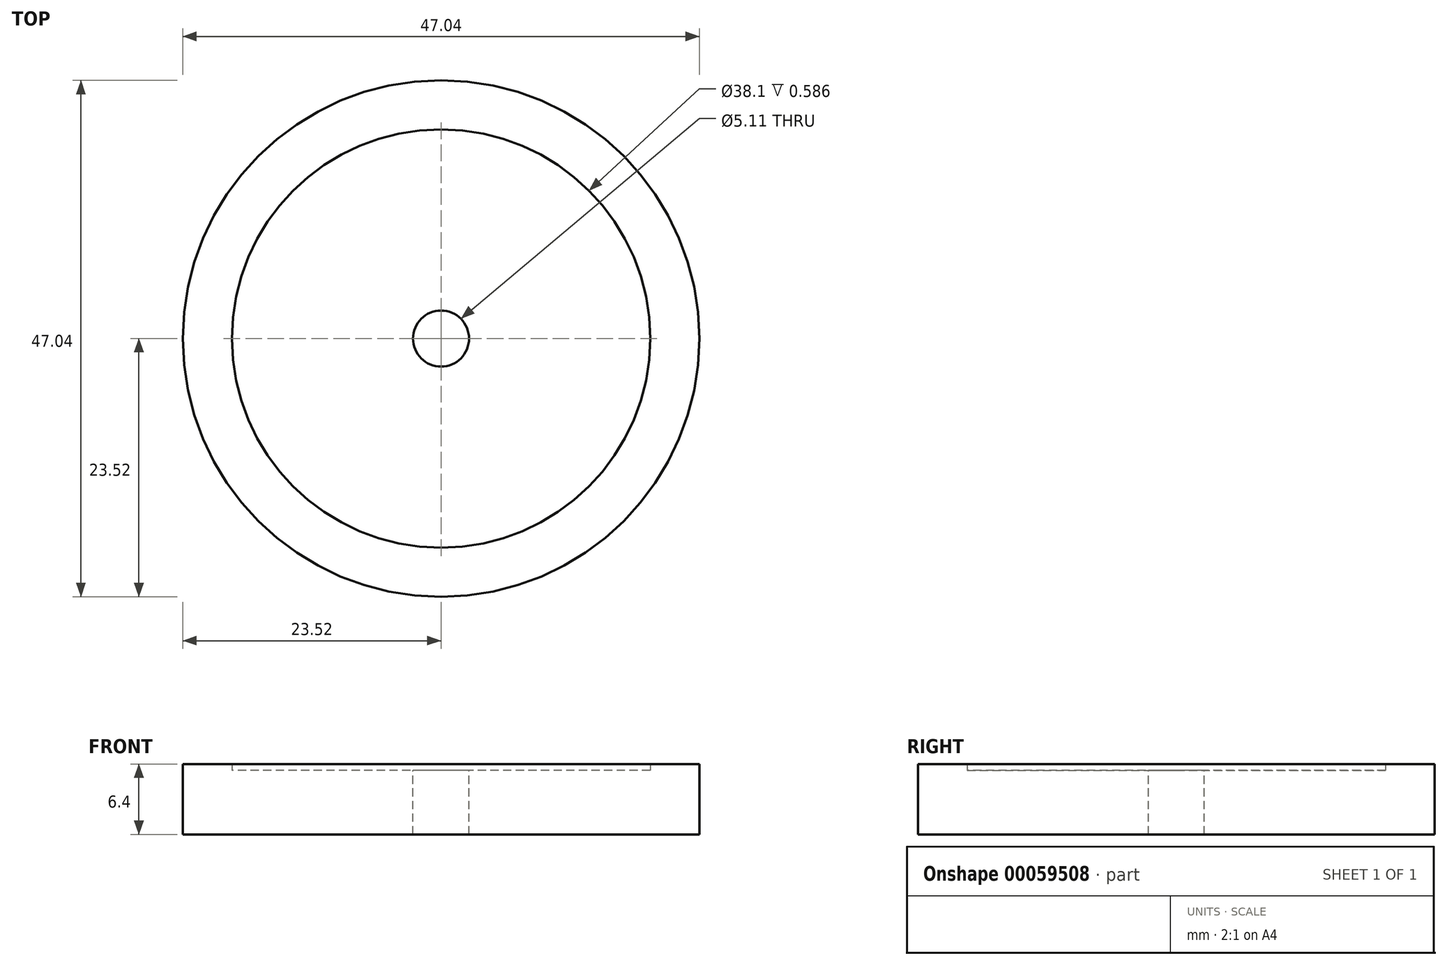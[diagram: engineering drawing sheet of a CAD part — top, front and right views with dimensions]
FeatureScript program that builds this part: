
annotation { "Feature Type Name" : "Feature", "Feature Type Description" : "" }
export const myFeature = defineFeature(function(context is Context, id is Id, definition is map)
    precondition{}
    {
        {
            var Q0;
            Q0=qCreatedBy(makeId("Top.planeOp"),FACE);
            var sketch = newSketch(context, id + "F0", { "sketchPlane" : qUnion([Q0])});
            skCircle(sketch, "E0", {"center": v(0, 0) * mm, "radius": 23.52 * mm});
            skCircle(sketch, "E1", {"center": v(0, 0) * mm, "radius": 19.05 * mm});
            skSolve(sketch);
        }
        {
            var Q0;
            Q0=makeQuery(id+"F0.imprint","IMPRINT",FACE,{"disambiguationData":[TD([[makeQuery(id+"F0.imprint","IMPRINT",EDGE,{"derivedFrom":sQuery(id+"F0.wireOp",EDGE,"E0")}),1.0]])]});
            extrude(context, id + "F1", {"entities" : qUnion([Q0]), "depth" : 6.4 * mm});
        }
        {
            var Q0;
            Q0=makeQuery(id+"F0.imprint","IMPRINT",FACE,{"disambiguationData":[TD([[makeQuery(id+"F0.imprint","IMPRINT",EDGE,{"derivedFrom":sQuery(id+"F0.wireOp",EDGE,"E1")}),1.0]])]});
            extrude(context, id + "F2", {"entities" : qUnion([Q0]), "operationType" : NewBodyOperationType.ADD, "depth" : (7 - (0.4 + 0.79)) * mm});
        }
        {
            var Q0;
            Q0=makeQuery(id+"F2.opExtrude","CAP_FACE",FACE,{"disambiguationData":[OSD([sQuery(id+"F0.wireOp",EDGE,"E1")])],"isStart":false});
            var sketch = newSketch(context, id + "F3", { "sketchPlane" : qUnion([Q0])});
            skCircle(sketch, "E2", {"center": v(0, 0) * mm, "radius": 2.55 * mm});
            skSolve(sketch);
        }
        {
            var Q0;
            Q0=makeQuery(id+"F3.imprint","IMPRINT",FACE,{"disambiguationData":[TD([[makeQuery(id+"F3.imprint","IMPRINT",EDGE,{"derivedFrom":sQuery(id+"F3.wireOp",EDGE,"E2")}),1.0]])]});
            extrude(context, id + "F4", {"entities" : qUnion([Q0]), "operationType" : NewBodyOperationType.REMOVE, "oppositeDirection" : true, "depth" : 12.7 * mm});
        }
    });
